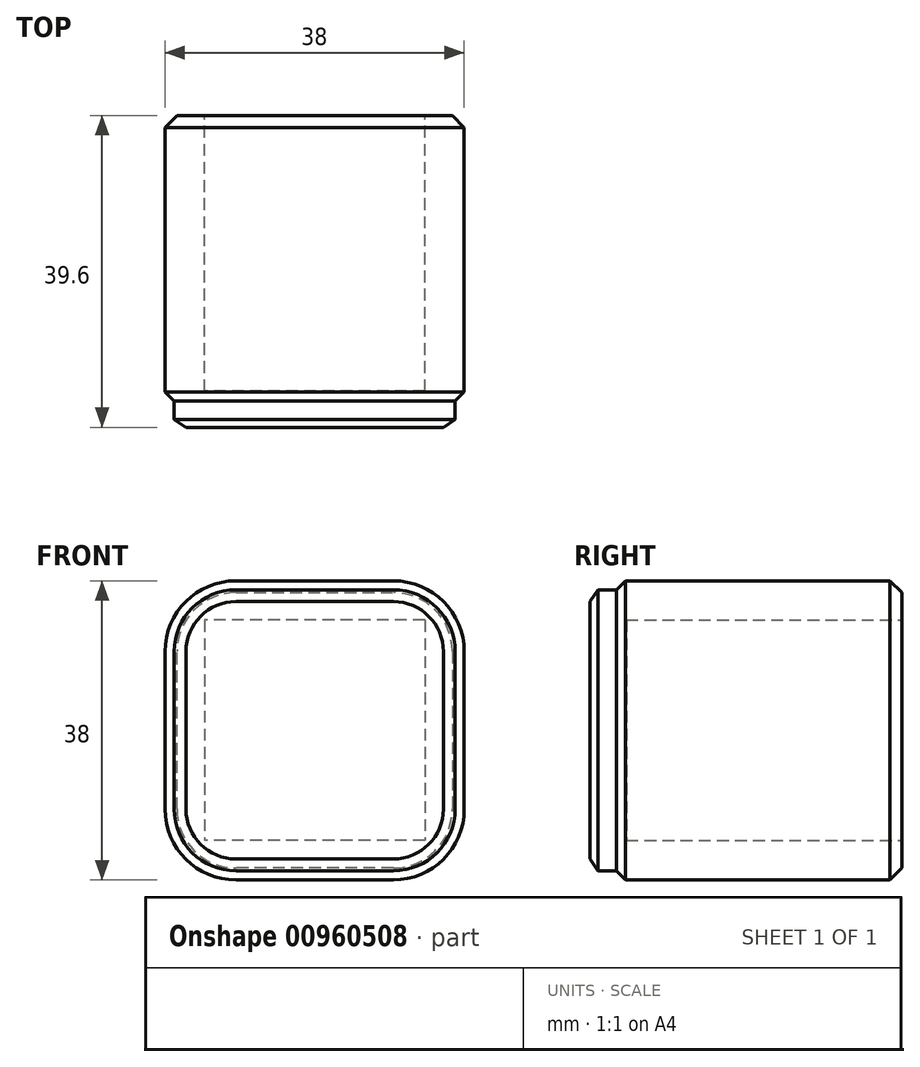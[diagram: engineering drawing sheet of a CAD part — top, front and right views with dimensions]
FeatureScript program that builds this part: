
annotation { "Feature Type Name" : "Feature", "Feature Type Description" : "" }
export const myFeature = defineFeature(function(context is Context, id is Id, definition is map)
    precondition{}
    {
        {
            var Q0;
            Q0=qCreatedBy(makeId("Front.planeOp"),FACE);
            var sketch = newSketch(context, id + "F0", { "sketchPlane" : qUnion([Q0])});
            skLineSegment(sketch, "E0.bottom", {"start": v(19, 19) * mm, "end": v(-19, 19) * mm});
            skLineSegment(sketch, "E0.top", {"start": v(19, -19) * mm, "end": v(-19, -19) * mm});
            skLineSegment(sketch, "E0.left", {"start": v(19, 19) * mm, "end": v(19, -19) * mm});
            skLineSegment(sketch, "E0.right", {"start": v(-19, 19) * mm, "end": v(-19, -19) * mm});
            skPoint(sketch, "E0.middle", {"position": v(0, 0) * mm});
            skLineSegment(sketch, "E1.0", {"start": v(17.85, 17.85) * mm, "end": v(-17.85, 17.85) * mm});
            skLineSegment(sketch, "E1.1", {"start": v(17.85, 17.85) * mm, "end": v(17.85, -17.85) * mm});
            skLineSegment(sketch, "E1.2", {"start": v(17.85, -17.85) * mm, "end": v(-17.85, -17.85) * mm});
            skLineSegment(sketch, "E1.3", {"start": v(-17.85, 17.85) * mm, "end": v(-17.85, -17.85) * mm});
            skSolve(sketch);
        }
        {
            var Q0;
            Q0=makeQuery(id+"F0.imprint","IMPRINT",FACE,{"disambiguationData":[TD([[makeQuery(id+"F0.imprint","IMPRINT",EDGE,{"derivedFrom":sQuery(id+"F0.wireOp",EDGE,"E0.bottom")}),1.0]])]});
            var Q1;
            Q1=makeQuery(id+"F0.imprint","IMPRINT",FACE,{"disambiguationData":[TD([[makeQuery(id+"F0.imprint","IMPRINT",EDGE,{"derivedFrom":sQuery(id+"F0.wireOp",EDGE,"E1.0")}),1.0]])]});
            extrude(context, id + "F1", {"entities" : qUnion([Q0, Q1]), "oppositeDirection" : true, "depth" : 36.6 * mm});
        }
        {
            var Q0;
            Q0=makeQuery(id+"F1.opExtrude","SWEPT_EDGE",EDGE,{"disambiguationData":[OSD([sQuery(id+"F0.wireOp",EDGE,"E0.bottom"),sQuery(id+"F0.wireOp",EDGE,"E0.left")])]});
            var Q1;
            Q1=makeQuery(id+"F1.opExtrude","SWEPT_EDGE",EDGE,{"disambiguationData":[OSD([sQuery(id+"F0.wireOp",EDGE,"E0.bottom"),sQuery(id+"F0.wireOp",EDGE,"E0.right")])]});
            var Q2;
            Q2=makeQuery(id+"F1.opExtrude","SWEPT_EDGE",EDGE,{"disambiguationData":[OSD([sQuery(id+"F0.wireOp",EDGE,"E0.top"),sQuery(id+"F0.wireOp",EDGE,"E0.left")])]});
            var Q3;
            Q3=makeQuery(id+"F1.opExtrude","SWEPT_EDGE",EDGE,{"disambiguationData":[OSD([sQuery(id+"F0.wireOp",EDGE,"E0.top"),sQuery(id+"F0.wireOp",EDGE,"E0.right")])]});
            fillet(context, id + "F2", {"entities" : qUnion([Q0, Q1, Q2, Q3]), "radius" : 9 * mm, "tangentPropagation" : true, "allowEdgeOverflow" : false});
        }
        {
            var Q0;
            Q0=makeQuery(id+"F0.imprint","IMPRINT",FACE,{"disambiguationData":[TD([[makeQuery(id+"F0.imprint","IMPRINT",EDGE,{"derivedFrom":sQuery(id+"F0.wireOp",EDGE,"E1.0")}),1.0]])]});
            extrude(context, id + "F3", {"entities" : qUnion([Q0]), "operationType" : NewBodyOperationType.ADD, "depth" : 3 * mm});
        }
        {
            var Q0;
            Q0=makeQuery(id+"F3.opExtrude","SWEPT_EDGE",EDGE,{"disambiguationData":[OSD([sQuery(id+"F0.wireOp",EDGE,"E1.0"),sQuery(id+"F0.wireOp",EDGE,"E1.1")])]});
            var Q1;
            Q1=makeQuery(id+"F3.opExtrude","SWEPT_EDGE",EDGE,{"disambiguationData":[OSD([sQuery(id+"F0.wireOp",EDGE,"E1.0"),sQuery(id+"F0.wireOp",EDGE,"E1.3")])]});
            var Q2;
            Q2=makeQuery(id+"F3.opExtrude","SWEPT_EDGE",EDGE,{"disambiguationData":[OSD([sQuery(id+"F0.wireOp",EDGE,"E1.2"),sQuery(id+"F0.wireOp",EDGE,"E1.3")])]});
            var Q3;
            Q3=makeQuery(id+"F3.opExtrude","SWEPT_EDGE",EDGE,{"disambiguationData":[OSD([sQuery(id+"F0.wireOp",EDGE,"E1.1"),sQuery(id+"F0.wireOp",EDGE,"E1.2")])]});
            fillet(context, id + "F4", {"entities" : qUnion([Q0, Q1, Q2, Q3]), "radius" : 7.85 * mm, "tangentPropagation" : true, "allowEdgeOverflow" : false});
        }
        {
            var Q0;
            Q0=makeQuery(id+"F1.opExtrude","CAP_FACE",FACE,{"disambiguationData":[OSD([sQuery(id+"F0.wireOp",EDGE,"E0.bottom"),sQuery(id+"F0.wireOp",EDGE,"E0.top"),sQuery(id+"F0.wireOp",EDGE,"E0.left"),sQuery(id+"F0.wireOp",EDGE,"E0.right")])],"isStart":false});
            var Q1;
            Q1=makeQuery(id+"F1.opExtrude","CAP_EDGE",EDGE,{"disambiguationData":[OSD([sQuery(id+"F0.wireOp",EDGE,"E0.bottom")])],"isStart":true});
            chamfer(context, id + "F5", {"entities" : qUnion([Q0, Q1]), "width" : 1.5 * mm, "tangentPropagation" : true});
        }
        {
            var Q0;
            Q0=makeQuery(id+"F3.opExtrude","CAP_FACE",FACE,{"disambiguationData":[OSD([sQuery(id+"F0.wireOp",EDGE,"E1.0"),sQuery(id+"F0.wireOp",EDGE,"E1.1"),sQuery(id+"F0.wireOp",EDGE,"E1.2"),sQuery(id+"F0.wireOp",EDGE,"E1.3")])],"isStart":false});
            chamfer(context, id + "F6", {"entities" : qUnion([Q0]), "chamferType" : ChamferType.TWO_OFFSETS, "width1" : 1.5 * mm, "oppositeDirection" : false, "width2" : 1 * mm, "tangentPropagation" : true});
        }
        {
            var Q0;
            Q0=makeQuery(id+"F1.opExtrude","CAP_FACE",FACE,{"disambiguationData":[OSD([sQuery(id+"F0.wireOp",EDGE,"E0.bottom"),sQuery(id+"F0.wireOp",EDGE,"E0.top"),sQuery(id+"F0.wireOp",EDGE,"E0.left"),sQuery(id+"F0.wireOp",EDGE,"E0.right")])],"isStart":false});
            var sketch = newSketch(context, id + "F7", { "sketchPlane" : qUnion([Q0])});
            skLineSegment(sketch, "E2.bottom", {"start": v(-14, 14) * mm, "end": v(14, 14) * mm});
            skLineSegment(sketch, "E2.top", {"start": v(-14, -14) * mm, "end": v(14, -14) * mm});
            skLineSegment(sketch, "E2.left", {"start": v(-14, 14) * mm, "end": v(-14, -14) * mm});
            skLineSegment(sketch, "E2.right", {"start": v(14, 14) * mm, "end": v(14, -14) * mm});
            skSolve(sketch);
        }
        {
            var Q0;
            Q0=makeQuery(id+"F7.imprint","IMPRINT",FACE,{"disambiguationData":[TD([[makeQuery(id+"F7.imprint","IMPRINT",EDGE,{"derivedFrom":sQuery(id+"F7.wireOp",EDGE,"E2.bottom")}),-1.0]])]});
            var Q1;
            Q1=makeQuery(id+"F3.opExtrude","CAP_FACE",FACE,{"disambiguationData":[OSD([sQuery(id+"F0.wireOp",EDGE,"E1.0"),sQuery(id+"F0.wireOp",EDGE,"E1.1"),sQuery(id+"F0.wireOp",EDGE,"E1.2"),sQuery(id+"F0.wireOp",EDGE,"E1.3")])],"isStart":false});
            extrude(context, id + "F8", {"entities" : qUnion([Q0]), "operationType" : NewBodyOperationType.REMOVE, "oppositeDirection" : true, "depth" : 35 * mm, "endBoundEntityFace" : qUnion([Q1]), "offsetDistance" : 25 * mm});
        }
    });
